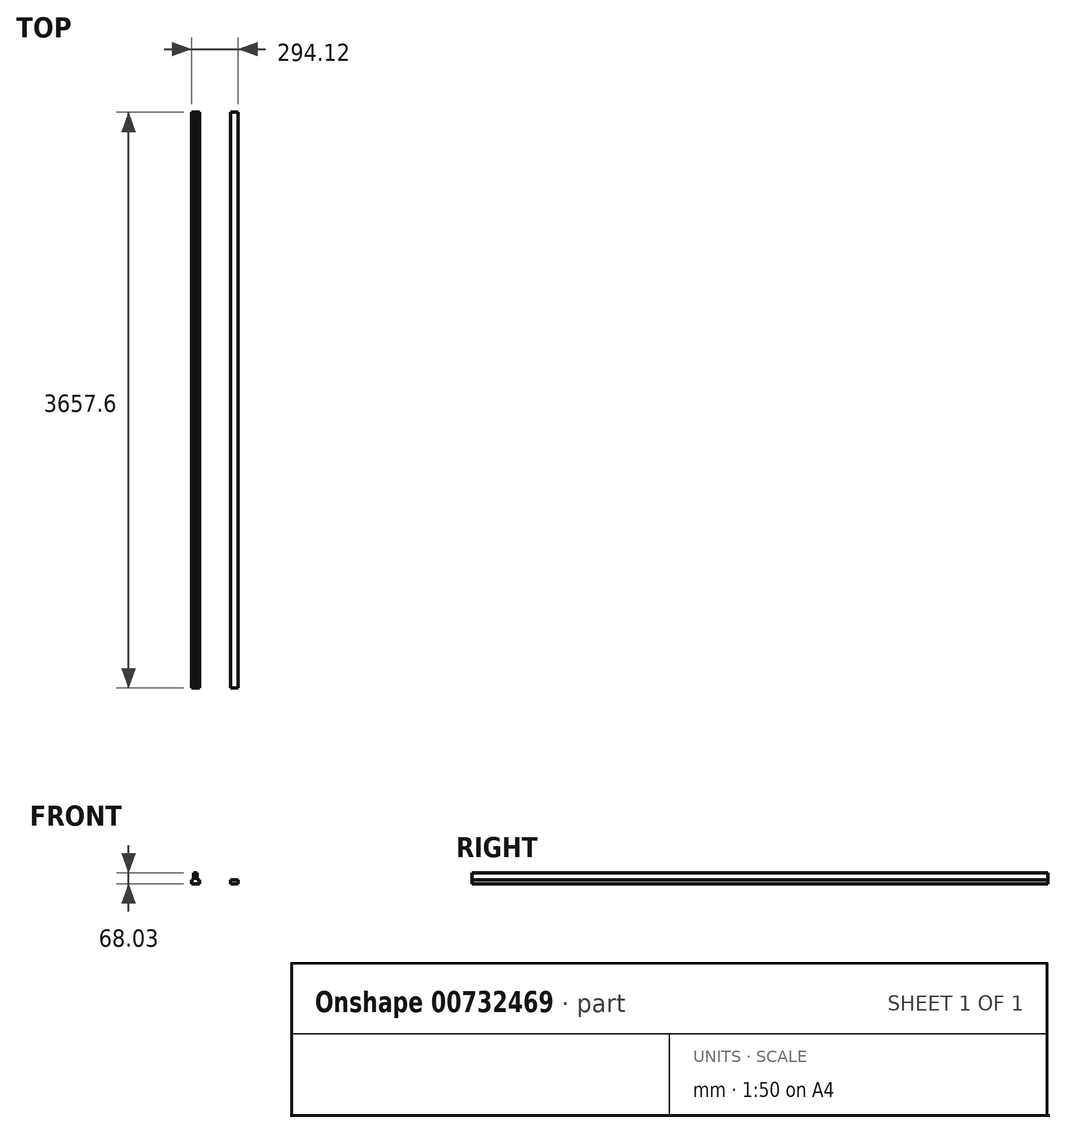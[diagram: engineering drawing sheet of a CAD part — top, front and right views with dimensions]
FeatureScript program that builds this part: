
annotation { "Feature Type Name" : "Feature", "Feature Type Description" : "" }
export const myFeature = defineFeature(function(context is Context, id is Id, definition is map)
    precondition{}
    {
        {
            var Q0;
            Q0=qCreatedBy(makeId("Front.planeOp"),FACE);
            var sketch = newSketch(context, id + "F0", { "sketchPlane" : qUnion([Q0])});
            skLineSegment(sketch, "E0.bottom", {"start": v(-150.6, 0) * mm, "end": v(-100.68, 0) * mm});
            skLineSegment(sketch, "E0.top", {"start": v(-150.6, -25.68) * mm, "end": v(-100.68, -25.68) * mm});
            skLineSegment(sketch, "E0.left", {"start": v(-150.6, 0) * mm, "end": v(-150.6, -25.68) * mm});
            skLineSegment(sketch, "E0.right", {"start": v(-100.68, 0) * mm, "end": v(-100.68, -25.68) * mm});
            skLineSegment(sketch, "E1.bottom", {"start": v(96.55, 0) * mm, "end": v(143.53, 0) * mm});
            skLineSegment(sketch, "E1.top", {"start": v(96.55, -25.68) * mm, "end": v(143.53, -25.68) * mm});
            skLineSegment(sketch, "E1.left", {"start": v(96.55, 0) * mm, "end": v(96.55, -25.68) * mm});
            skLineSegment(sketch, "E1.right", {"start": v(143.53, 0) * mm, "end": v(143.53, -25.68) * mm});
            skLineSegment(sketch, "E2.bottom", {"start": v(-100.68, -12.84) * mm, "end": v(96.55, -12.84) * mm});
            skLineSegment(sketch, "E2.top", {"start": v(-100.68, -25.68) * mm, "end": v(96.55, -25.68) * mm});
            skLineSegment(sketch, "E2.left", {"start": v(-100.68, -12.84) * mm, "end": v(-100.68, -25.68) * mm});
            skLineSegment(sketch, "E2.right", {"start": v(96.55, -12.84) * mm, "end": v(96.55, -25.68) * mm});
            skLineSegment(sketch, "E3.bottom", {"start": v(143.53, -18.34) * mm, "end": v(178.28, -18.34) * mm});
            skLineSegment(sketch, "E3.top", {"start": v(143.53, -25.68) * mm, "end": v(178.28, -25.68) * mm});
            skLineSegment(sketch, "E3.left", {"start": v(143.53, -18.34) * mm, "end": v(143.53, -25.68) * mm});
            skLineSegment(sketch, "E3.right", {"start": v(178.28, -18.34) * mm, "end": v(178.28, -25.68) * mm});
            skPoint(sketch, "E4.firstSnap0", {"position": v(-100.68, -19.26) * mm});
            skLineSegment(sketch, "E4.bottom", {"start": v(-150.6, -19.26) * mm, "end": v(-186.8, -19.26) * mm});
            skLineSegment(sketch, "E4.top", {"start": v(-150.6, -25.68) * mm, "end": v(-186.8, -25.68) * mm});
            skLineSegment(sketch, "E4.left", {"start": v(-150.6, -19.26) * mm, "end": v(-150.6, -25.68) * mm});
            skLineSegment(sketch, "E4.right", {"start": v(-186.8, -19.26) * mm, "end": v(-186.8, -25.68) * mm});
            skLineSegment(sketch, "E5.bottom", {"start": v(109.76, 38.43) * mm, "end": v(130.32, 38.43) * mm});
            skLineSegment(sketch, "E5.top", {"start": v(109.76, 0) * mm, "end": v(130.32, 0) * mm});
            skLineSegment(sketch, "E5.left", {"start": v(109.76, 38.43) * mm, "end": v(109.76, 0) * mm});
            skLineSegment(sketch, "E5.right", {"start": v(130.32, 38.43) * mm, "end": v(130.32, 0) * mm});
            skLineSegment(sketch, "E6.bottom", {"start": v(-138.36, 42.35) * mm, "end": v(-116.83, 42.35) * mm});
            skLineSegment(sketch, "E6.top", {"start": v(-138.36, 0) * mm, "end": v(-116.83, 0) * mm});
            skLineSegment(sketch, "E6.left", {"start": v(-138.36, 42.35) * mm, "end": v(-138.36, 0) * mm});
            skLineSegment(sketch, "E6.right", {"start": v(-116.83, 42.35) * mm, "end": v(-116.83, 0) * mm});
            skSolve(sketch);
        }
        {
            var Q0;
            Q0=makeQuery(id+"F0.imprint","IMPRINT",FACE,{"disambiguationData":[TD([[makeQuery(id+"F0.imprint","IMPRINT",EDGE,{"derivedFrom":sQuery(id+"F0.wireOp",EDGE,"E6.bottom")}),-1.0]])]});
            var Q1;
            Q1=makeQuery(id+"F0.imprint","IMPRINT",FACE,{"disambiguationData":[TD([[makeQuery(id+"F0.imprint","IMPRINT",EDGE,{"derivedFrom":sQuery(id+"F0.wireOp",EDGE,"E0.top")}),1.0]])]});
            var Q2;
            Q2=makeQuery(id+"F0.imprint","IMPRINT",FACE,{"disambiguationData":[TD([[makeQuery(id+"F0.imprint","IMPRINT",EDGE,{"derivedFrom":sQuery(id+"F0.wireOp",EDGE,"E1.top")}),1.0]])]});
            extrude(context, id + "F1", {"entities" : qUnion([Q0, Q1, Q2]), "depth" : 3657.6 * mm, "offsetDistance" : 25.4 * mm});
        }
    });
